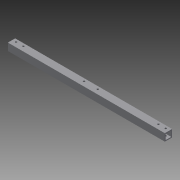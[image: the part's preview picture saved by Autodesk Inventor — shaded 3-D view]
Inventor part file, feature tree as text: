
AUTODESK INVENTOR PART (.ipt)
format: ipt  version: 2015 SP1 (Build 190203100, 203)  size: 128,000 bytes
history: native  units: in
note: dims shown in document units (in); Inventor stores cm internally (conversion verified against a paired STEP export)
features: sketch x3, hole x2, projected_geometry x2, extrude x1
ambient origin geometry x8: Origin, YZ Plane, XZ Plane, XY Plane, X Axis, Y Axis, Z Axis, Center Point
bodies: Solid1 (feature_tree)
feature tree (8):
  extrude  "Extrusion1"  Depth=1.0in
  hole  "Hole1"  [1 undecoded]
  hole  "Hole4"  [1 undecoded]
  sketch  "Sketch1"  dims[d0=1.0in d1=1.0in]
  sketch  "Sketch2"  dims[d2=0.75in d3=0.75in]
  projected_geometry  "Projected Loop1"
  sketch  "Sketch3"  dims[d4=0.125in d5=0.125in d6=21.5in d7=0.0in d8=0.625in d9=0.5in d10=0.5in d11=0.625in d12=0.25in d13=0.75in d14=0.375in d15=0.25in d16=0.5635in d17=1.0in d18=0.8108in d19=1.5in d20=1.5in d21=0.625in d22=0.625in d30=0.625in d31=9.8125in d39=9.8125in d40=0.625in d41=0.25in d42=0.75in d43=0.375in d44=0.25in d45=0.5635in d46=1.0in d47=0.8108in]
  projected_geometry  "Projected Loop2"
note: 2 required parameter values undecoded (feature->parameter linkage not recoverable at this tier; creation-order binding heuristic only, values carry confidence <= 0.55)
